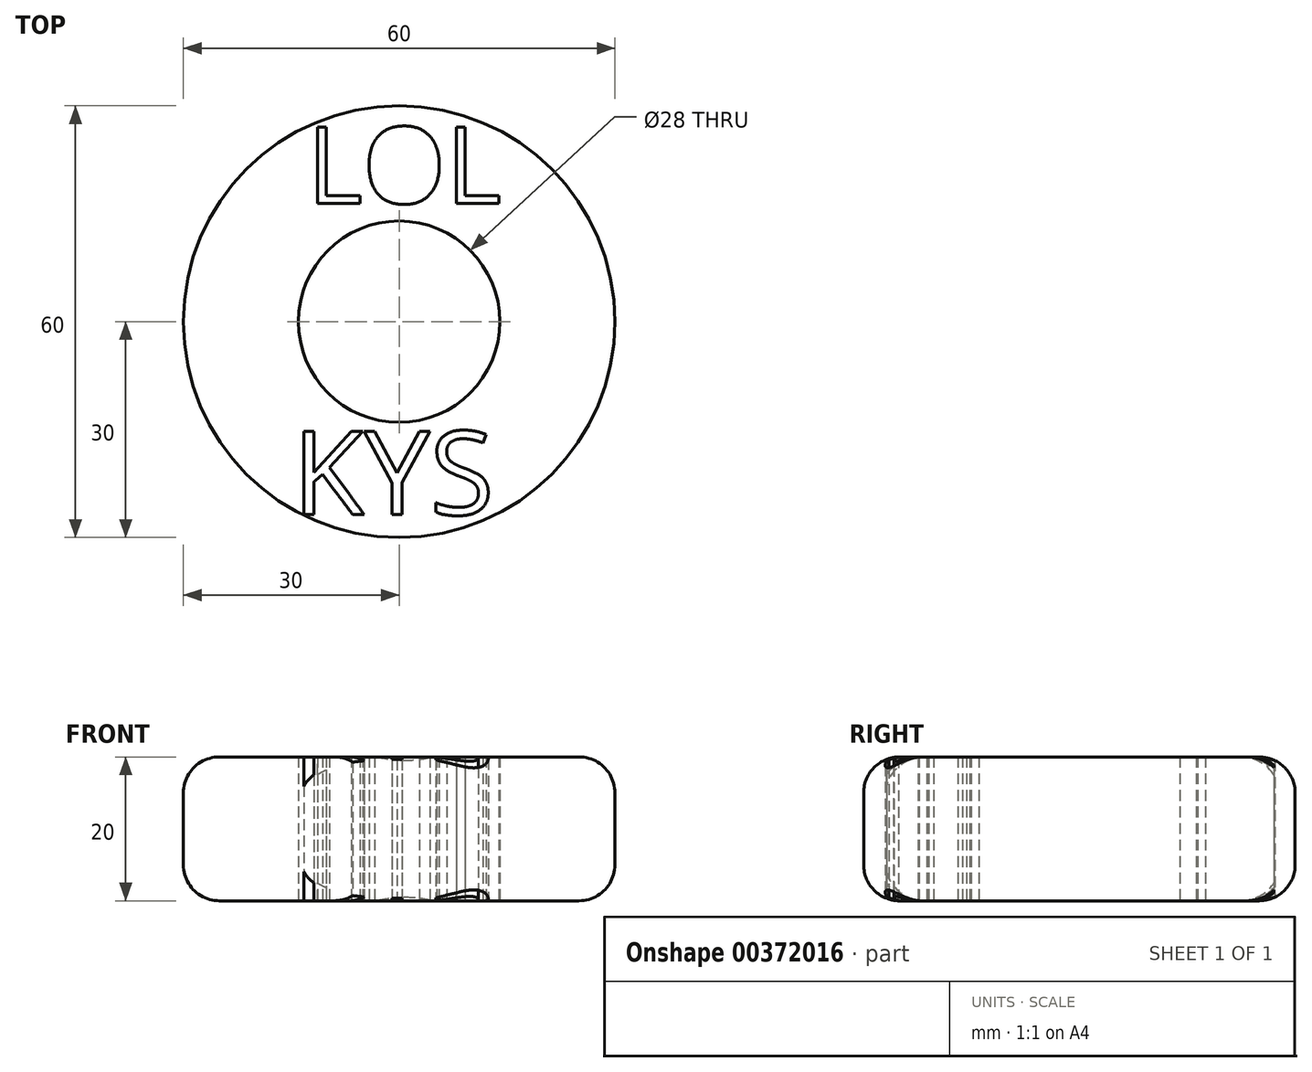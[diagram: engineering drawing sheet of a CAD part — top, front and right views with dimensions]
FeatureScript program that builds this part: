
annotation { "Feature Type Name" : "Feature", "Feature Type Description" : "" }
export const myFeature = defineFeature(function(context is Context, id is Id, definition is map)
    precondition{}
    {
        {
            var Q0;
            Q0=qCreatedBy(makeId("Top.planeOp"),FACE);
            var sketch = newSketch(context, id + "F0", { "sketchPlane" : qUnion([Q0])});
            skCircle(sketch, "E0", {"center": v(0, 0) * mm, "radius": 30 * mm});
            skCircle(sketch, "E1", {"center": v(0, 0) * mm, "radius": 14 * mm});
            skText(sketch, "E2", { "text": "LOL", "fontName": "OpenSans-Regular.ttf"});
            skText(sketch, "E3", { "text": "KYS", "fontName": "OpenSans-Regular.ttf"});
            const initialGuessF0  = {"E2": [-0.0128, 0.01643, 1, 0, 0.0107], "E3": [-0.01482, -0.02683, 1, 0, 0.0117]};
            skSetInitialGuess(sketch, initialGuessF0);
            skSolve(sketch);
        }
        {
            var Q0;
            Q0=makeQuery(id+"F0.imprint","IMPRINT",FACE,{"disambiguationData":[TD([[makeQuery(id+"F0.imprint","IMPRINT",EDGE,{"derivedFrom":sQuery(id+"F0.wireOp",EDGE,"E0")}),1.0]])]});
            extrude(context, id + "F1", {"entities" : qUnion([Q0]), "depth" : 20 * mm});
        }
        {
            var Q0;
            Q0=makeQuery(id+"F1.opExtrude","SWEPT_FACE",FACE,{"disambiguationData":[OSD([sQuery(id+"F0.wireOp",EDGE,"E0")])]});
            fillet(context, id + "F2", {"entities" : qUnion([Q0]), "radius" : 5 * mm, "tangentPropagation" : true, "allowEdgeOverflow" : false});
        }
    });
